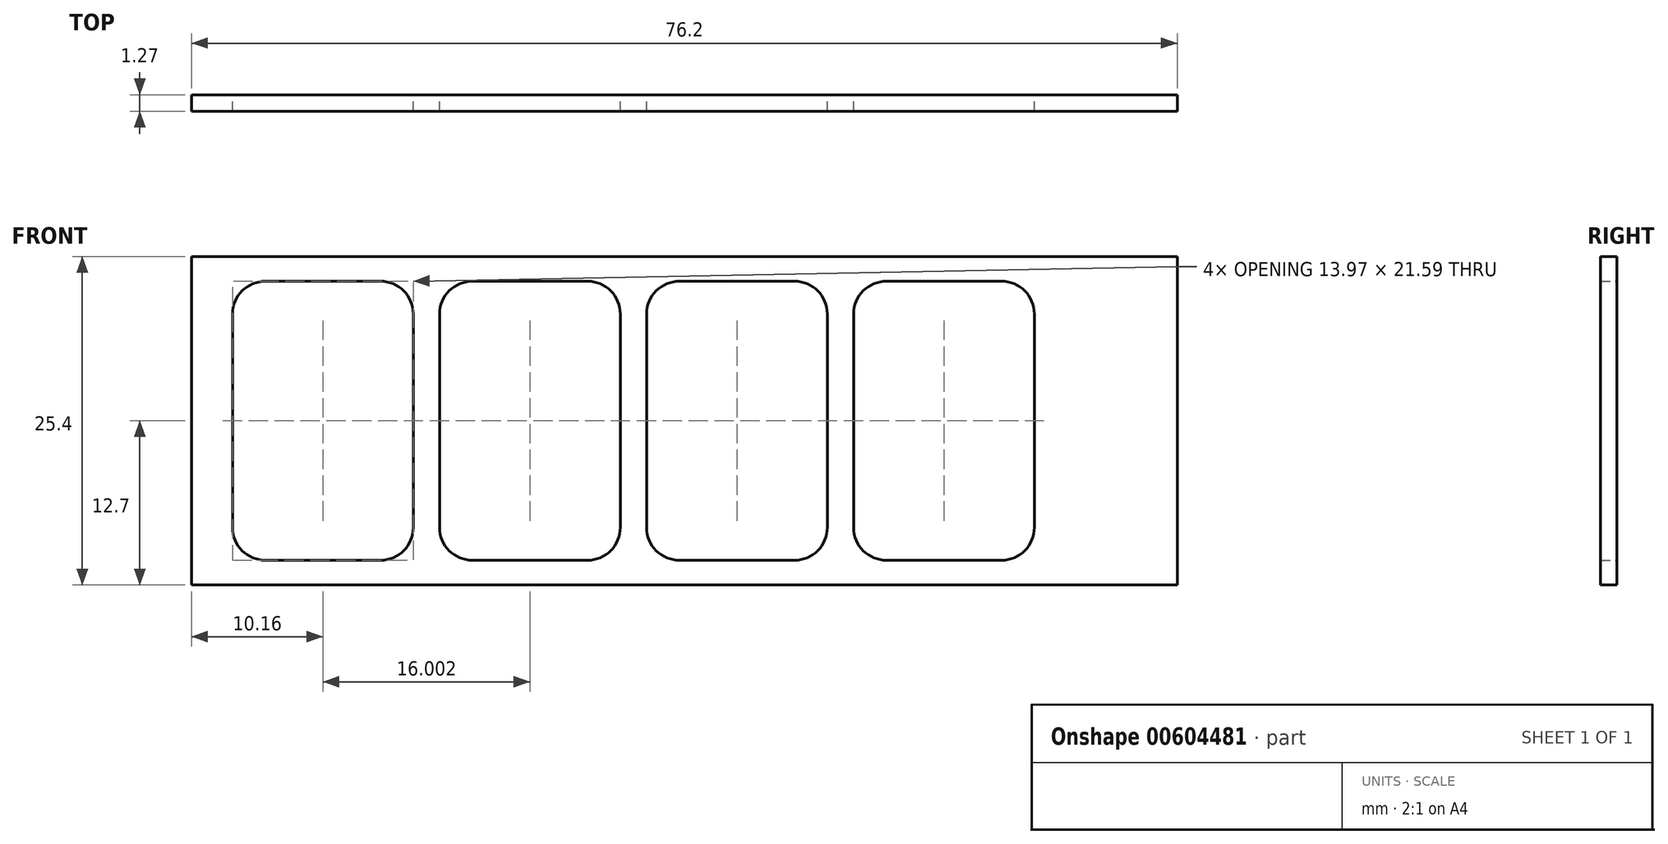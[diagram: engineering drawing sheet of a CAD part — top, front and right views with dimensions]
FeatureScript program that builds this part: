
annotation { "Feature Type Name" : "Feature", "Feature Type Description" : "" }
export const myFeature = defineFeature(function(context is Context, id is Id, definition is map)
    precondition{}
    {
        {
            var Q0;
            Q0=qCreatedBy(makeId("Front.planeOp"),FACE);
            var sketch = newSketch(context, id + "F0", { "sketchPlane" : qUnion([Q0])});
            skLineSegment(sketch, "E0.bottom", {"start": v(-38.1, 12.7) * mm, "end": v(38.1, 12.7) * mm});
            skLineSegment(sketch, "E0.top", {"start": v(-38.1, -12.7) * mm, "end": v(38.1, -12.7) * mm});
            skLineSegment(sketch, "E0.left", {"start": v(-38.1, 12.7) * mm, "end": v(-38.1, -12.7) * mm});
            skLineSegment(sketch, "E0.right", {"start": v(38.1, 12.7) * mm, "end": v(38.1, -12.7) * mm});
            skPoint(sketch, "E0.middle", {"position": v(0, 0) * mm});
            skLineSegment(sketch, "E1.bottom", {"start": v(-32.39, 10.8) * mm, "end": v(-23.5, 10.8) * mm});
            skLineSegment(sketch, "E1.top", {"start": v(-32.39, -10.8) * mm, "end": v(-23.5, -10.8) * mm});
            skLineSegment(sketch, "E1.left", {"start": v(-34.93, 8.26) * mm, "end": v(-34.93, -8.26) * mm});
            skLineSegment(sketch, "E1.right", {"start": v(-20.95, 8.26) * mm, "end": v(-20.95, -8.26) * mm});
            skPoint(sketch, "E1.middle", {"position": v(-27.94, 0) * mm});
            skLineSegment(sketch, "E2.bottom", {"start": v(-16.38, 10.8) * mm, "end": v(-7.5, 10.8) * mm});
            skLineSegment(sketch, "E2.top", {"start": v(-16.38, -10.8) * mm, "end": v(-7.5, -10.8) * mm});
            skLineSegment(sketch, "E2.left", {"start": v(-18.92, 8.26) * mm, "end": v(-18.92, -8.26) * mm});
            skLineSegment(sketch, "E2.right", {"start": v(-4.95, 8.26) * mm, "end": v(-4.95, -8.26) * mm});
            skPoint(sketch, "E2.middle", {"position": v(-11.94, 0) * mm});
            skLineSegment(sketch, "E3.bottom", {"start": v(-0.38, 10.8) * mm, "end": v(8.5, 10.8) * mm});
            skLineSegment(sketch, "E3.top", {"start": v(-0.38, -10.8) * mm, "end": v(8.5, -10.8) * mm});
            skLineSegment(sketch, "E3.left", {"start": v(-2.92, 8.25) * mm, "end": v(-2.92, -8.26) * mm});
            skLineSegment(sketch, "E3.right", {"start": v(11.05, 8.26) * mm, "end": v(11.05, -8.26) * mm});
            skPoint(sketch, "E3.middle", {"position": v(4.06, 0) * mm});
            skLineSegment(sketch, "E4.bottom", {"start": v(15.62, 10.8) * mm, "end": v(24.51, 10.8) * mm});
            skLineSegment(sketch, "E4.top", {"start": v(15.62, -10.8) * mm, "end": v(24.51, -10.8) * mm});
            skLineSegment(sketch, "E4.left", {"start": v(13.08, 8.25) * mm, "end": v(13.08, -8.25) * mm});
            skLineSegment(sketch, "E4.right", {"start": v(27.05, 8.26) * mm, "end": v(27.05, -8.25) * mm});
            skPoint(sketch, "E4.middle", {"position": v(20.07, 0) * mm});
            skPoint(sketch, "E5.visualSharp", {"position": v(-20.95, 10.8) * mm});
            skArc(sketch, "E5.filletArc", {"start": v(-20.95, 8.26) * mm, "mid": v(-21.7, 10.05) * mm, "end": v(-23.5, 10.8) * mm});
            skPoint(sketch, "E6.visualSharp", {"position": v(-34.92, 10.8) * mm});
            skArc(sketch, "E6.filletArc", {"start": v(-32.39, 10.8) * mm, "mid": v(-34.18, 10.05) * mm, "end": v(-34.93, 8.26) * mm});
            skPoint(sketch, "E7.visualSharp", {"position": v(-34.93, -10.8) * mm});
            skArc(sketch, "E7.filletArc", {"start": v(-34.92, -8.26) * mm, "mid": v(-34.18, -10.05) * mm, "end": v(-32.39, -10.8) * mm});
            skPoint(sketch, "E8.visualSharp", {"position": v(-20.96, -10.8) * mm});
            skArc(sketch, "E8.filletArc", {"start": v(-23.5, -10.8) * mm, "mid": v(-21.7, -10.05) * mm, "end": v(-20.95, -8.26) * mm});
            skPoint(sketch, "E9.visualSharp", {"position": v(-18.92, 10.8) * mm});
            skArc(sketch, "E9.filletArc", {"start": v(-16.38, 10.8) * mm, "mid": v(-18.18, 10.05) * mm, "end": v(-18.92, 8.26) * mm});
            skPoint(sketch, "E10.visualSharp", {"position": v(-4.95, 10.8) * mm});
            skArc(sketch, "E10.filletArc", {"start": v(-4.95, 8.26) * mm, "mid": v(-5.7, 10.05) * mm, "end": v(-7.5, 10.8) * mm});
            skPoint(sketch, "E11.visualSharp", {"position": v(-4.95, -10.8) * mm});
            skArc(sketch, "E11.filletArc", {"start": v(-7.5, -10.8) * mm, "mid": v(-5.7, -10.05) * mm, "end": v(-4.95, -8.26) * mm});
            skPoint(sketch, "E12.visualSharp", {"position": v(-18.92, -10.8) * mm});
            skArc(sketch, "E12.filletArc", {"start": v(-18.92, -8.26) * mm, "mid": v(-18.18, -10.05) * mm, "end": v(-16.38, -10.8) * mm});
            skPoint(sketch, "E13.visualSharp", {"position": v(-2.92, 10.8) * mm});
            skArc(sketch, "E13.filletArc", {"start": v(-0.38, 10.8) * mm, "mid": v(-2.18, 10.05) * mm, "end": v(-2.92, 8.26) * mm});
            skPoint(sketch, "E14.visualSharp", {"position": v(11.05, 10.8) * mm});
            skArc(sketch, "E14.filletArc", {"start": v(11.05, 8.26) * mm, "mid": v(10.3, 10.05) * mm, "end": v(8.5, 10.8) * mm});
            skPoint(sketch, "E15.visualSharp", {"position": v(11.05, -10.8) * mm});
            skArc(sketch, "E15.filletArc", {"start": v(8.5, -10.8) * mm, "mid": v(10.3, -10.05) * mm, "end": v(11.05, -8.26) * mm});
            skPoint(sketch, "E16.visualSharp", {"position": v(-2.92, -10.8) * mm});
            skArc(sketch, "E16.filletArc", {"start": v(-2.92, -8.26) * mm, "mid": v(-2.18, -10.05) * mm, "end": v(-0.38, -10.8) * mm});
            skPoint(sketch, "E17.visualSharp", {"position": v(13.08, -10.8) * mm});
            skArc(sketch, "E17.filletArc", {"start": v(13.08, -8.25) * mm, "mid": v(13.82, -10.05) * mm, "end": v(15.62, -10.8) * mm});
            skPoint(sketch, "E18.visualSharp", {"position": v(13.08, 10.8) * mm});
            skArc(sketch, "E18.filletArc", {"start": v(15.62, 10.8) * mm, "mid": v(13.82, 10.05) * mm, "end": v(13.08, 8.26) * mm});
            skPoint(sketch, "E19.visualSharp", {"position": v(27.05, 10.8) * mm});
            skArc(sketch, "E19.filletArc", {"start": v(27.05, 8.26) * mm, "mid": v(26.3, 10.05) * mm, "end": v(24.51, 10.8) * mm});
            skPoint(sketch, "E20.visualSharp", {"position": v(27.05, -10.8) * mm});
            skArc(sketch, "E20.filletArc", {"start": v(24.51, -10.8) * mm, "mid": v(26.3, -10.05) * mm, "end": v(27.05, -8.25) * mm});
            skSolve(sketch);
        }
        {
            var Q0;
            Q0 = qSketchRegion(id + "F0", true);
            extrude(context, id + "F1", {"entities" : qUnion([Q0]), "depth" : 1.27 * mm, "offsetDistance" : 25.4 * mm});
        }
    });
